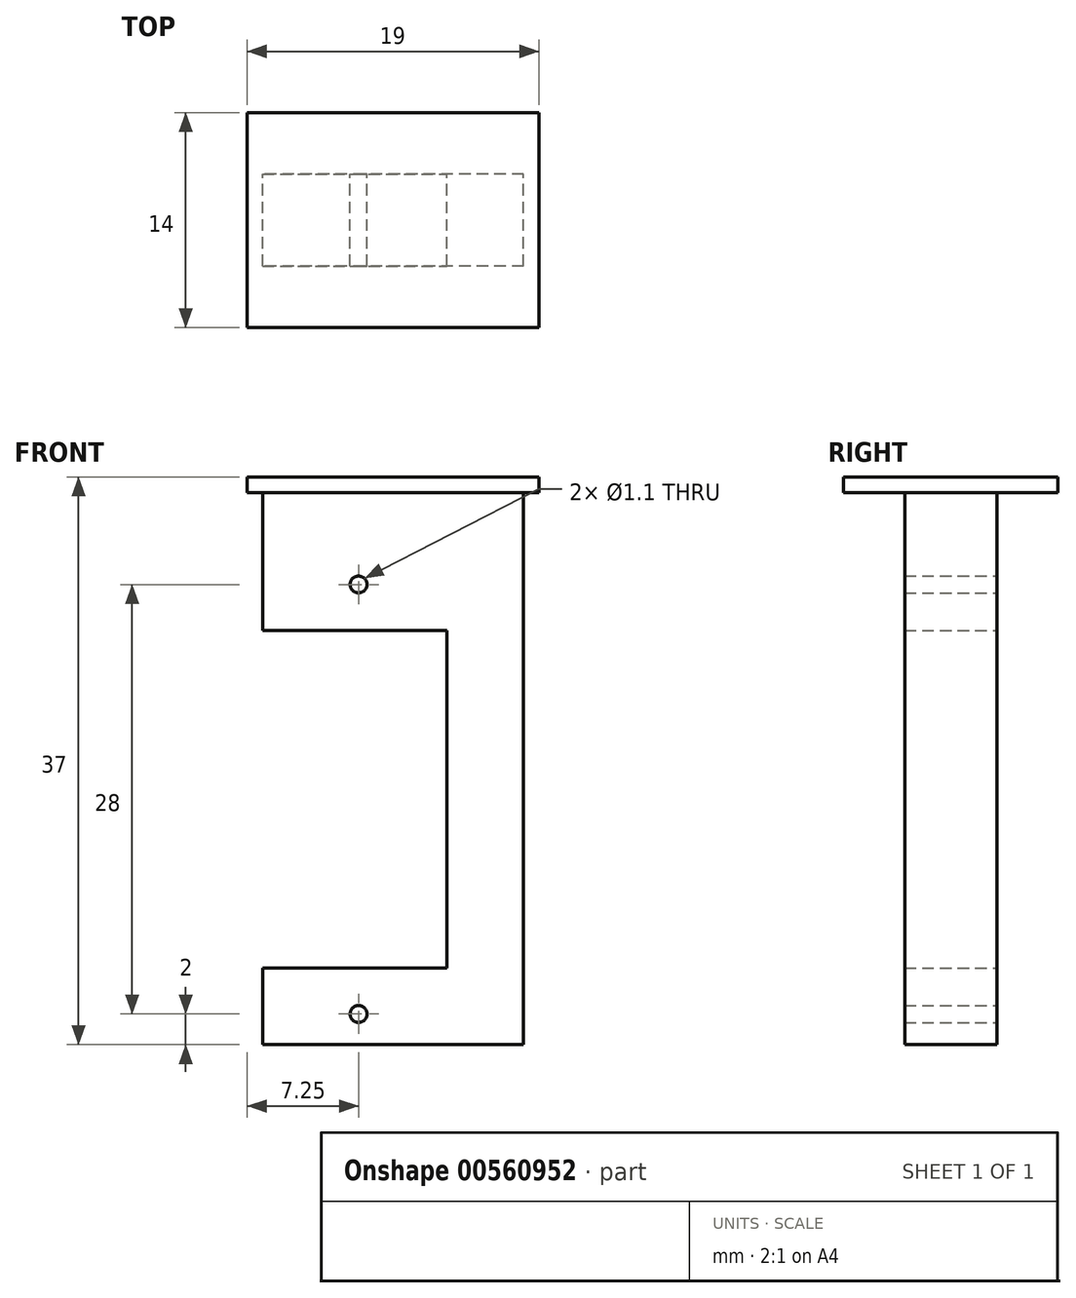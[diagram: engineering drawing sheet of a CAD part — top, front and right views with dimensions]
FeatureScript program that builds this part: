
annotation { "Feature Type Name" : "Feature", "Feature Type Description" : "" }
export const myFeature = defineFeature(function(context is Context, id is Id, definition is map)
    precondition{}
    {
        {
            var Q0;
            Q0=qCreatedBy(makeId("Front.planeOp"),FACE);
            var sketch = newSketch(context, id + "F0", { "sketchPlane" : qUnion([Q0])});
            skLineSegment(sketch, "E0.bottom", {"start": v(0, 0) * mm, "end": v(12, 0) * mm});
            skLineSegment(sketch, "E0.top", {"start": v(0, 5) * mm, "end": v(12, 5) * mm});
            skLineSegment(sketch, "E0.left", {"start": v(0, 0) * mm, "end": v(0, 5) * mm});
            skLineSegment(sketch, "E1.bottom", {"start": v(12, 5) * mm, "end": v(17, 5) * mm});
            skLineSegment(sketch, "E1.top", {"start": v(12, -27) * mm, "end": v(17, -27) * mm});
            skLineSegment(sketch, "E1.left", {"start": v(12, 0) * mm, "end": v(12, -22) * mm});
            skLineSegment(sketch, "E1.right", {"start": v(17, 5) * mm, "end": v(17, -27) * mm});
            skLineSegment(sketch, "E2.bottom", {"start": v(12, -27) * mm, "end": v(0, -27) * mm});
            skLineSegment(sketch, "E2.top", {"start": v(12, -22) * mm, "end": v(0, -22) * mm});
            skLineSegment(sketch, "E2.right", {"start": v(0, -27) * mm, "end": v(0, -22) * mm});
            skCircle(sketch, "E3", {"center": v(6.25, 3) * mm, "radius": 0.55 * mm});
            skCircle(sketch, "E4", {"center": v(6.25, -25) * mm, "radius": 0.55 * mm});
            skSolve(sketch);
        }
        {
            var Q0;
            Q0 = qSketchRegion(id + "F0", true);
            extrude(context, id + "F1", {"entities" : qUnion([Q0]), "depth" : 6 * mm, "offsetDistance" : 25 * mm});
        }
        {
            var Q0;
            Q0=makeQuery(id+"F1.opExtrude","SWEPT_FACE",FACE,{"disambiguationData":[OSD([sQuery(id+"F0.wireOp",EDGE,"E0.top"),sQuery(id+"F0.wireOp",EDGE,"E1.bottom")])]});
            extrude(context, id + "F2", {"entities" : qUnion([Q0]), "operationType" : NewBodyOperationType.ADD, "depth" : 4 * mm, "offsetDistance" : 25 * mm});
        }
        {
            var Q0;
            Q0=makeQuery(id+"F2.opExtrude","CAP_FACE",FACE,{"disambiguationData":[OSD([sQuery(id+"F0.wireOp",EDGE,"E0.top"),sQuery(id+"F0.wireOp",EDGE,"E1.bottom")])],"isStart":false});
            var sketch = newSketch(context, id + "F3", { "sketchPlane" : qUnion([Q0])});
            skLineSegment(sketch, "E5.bottom", {"start": v(-1, -10) * mm, "end": v(18, -10) * mm});
            skLineSegment(sketch, "E5.top", {"start": v(-1, 4) * mm, "end": v(18, 4) * mm});
            skLineSegment(sketch, "E5.left", {"start": v(-1, -10) * mm, "end": v(-1, 4) * mm});
            skLineSegment(sketch, "E5.right", {"start": v(18, -10) * mm, "end": v(18, 4) * mm});
            skSolve(sketch);
        }
        {
            var Q0;
            Q0=makeQuery(id+"F3.imprint","IMPRINT",FACE,{"disambiguationData":[TD([[makeQuery(id+"F3.imprint","IMPRINT",EDGE,{"derivedFrom":sQuery(id+"F3.wireOp",EDGE,"E5.bottom")}),1.0]])]});
            var Q1;
            {var subQ0=sQuery(id+"F0.wireOp",EDGE,"E0.top");Q1=makeQuery(id+"F3.imprint","IMPRINT",FACE,{"disambiguationData":[TD([[makeQuery(id+"F3.imprint","IMPRINT",EDGE,{"derivedFrom":makeQuery(id+"F2.opExtrude","CAP_EDGE",EDGE,{"disambiguationData":[OSD([subQ0,sQuery(id+"F0.wireOp",EDGE,"E0.left")])],"isStart":false})}),-1.0]])]});}
            extrude(context, id + "F4", {"entities" : qUnion([Q0, Q1]), "operationType" : NewBodyOperationType.ADD, "depth" : 1 * mm, "offsetDistance" : 25 * mm});
        }
    });
